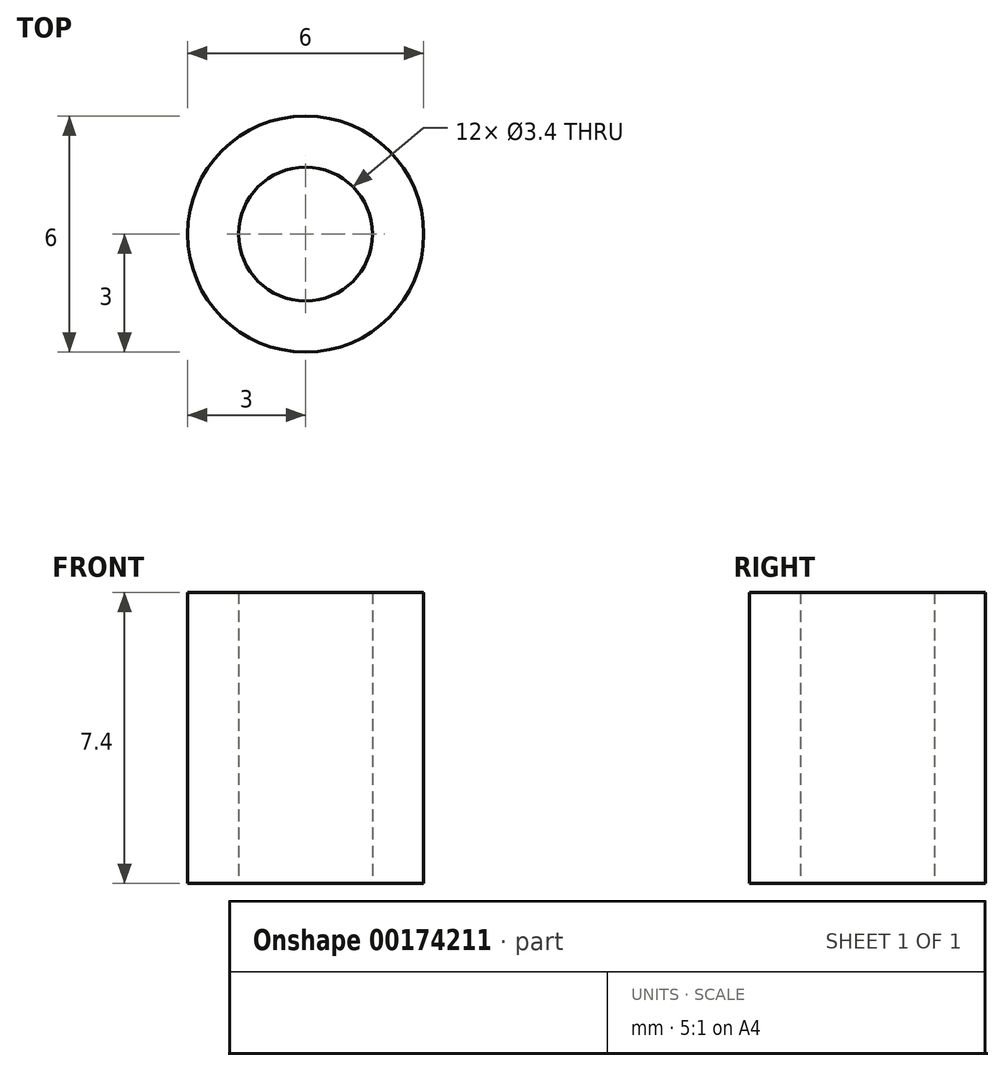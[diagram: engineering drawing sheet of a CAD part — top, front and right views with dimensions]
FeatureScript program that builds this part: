
annotation { "Feature Type Name" : "Feature", "Feature Type Description" : "" }
export const myFeature = defineFeature(function(context is Context, id is Id, definition is map)
    precondition{}
    {
        {
            var Q0;
            Q0=qCreatedBy(makeId("Top.planeOp"),FACE);
            var sketch = newSketch(context, id + "F0", { "sketchPlane" : qUnion([Q0])});
            skCircle(sketch, "E0", {"center": v(0, 0) * mm, "radius": 3 * mm});
            skCircle(sketch, "E1", {"center": v(0, 0) * mm, "radius": 1.7 * mm});
            skSolve(sketch);
        }
        {
            var Q0;
            Q0=makeQuery(id+"F0.imprint","IMPRINT",FACE,{"disambiguationData":[TD([[makeQuery(id+"F0.imprint","IMPRINT",EDGE,{"derivedFrom":sQuery(id+"F0.wireOp",EDGE,"E0")}),1.0]])]});
            extrude(context, id + "F1", {"entities" : qUnion([Q0]), "depth" : 7.4 * mm, "offsetDistance" : 25 * mm});
        }
    });
